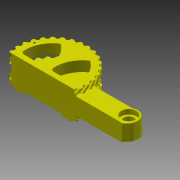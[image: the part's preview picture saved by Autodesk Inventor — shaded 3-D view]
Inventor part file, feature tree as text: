
AUTODESK INVENTOR PART (.ipt)
format: ipt  version: 2013 (Build 170138000, 138)  size: 5,737,472 bytes
history: native  units: mm
features: extrude x13, sketch x13, other x3, fillet x1
ambient origin geometry x8: Origin, YZ Plane, XZ Plane, XY Plane, X Axis, Y Axis, Z Axis, Center Point
bodies: Solid1 (feature_tree)
feature tree (30):
  other  "_GEARS.iam"
  other  "gear.ipt:1"
  other  "gear.ipt:2"
  extrude  "Extrusion1"  Depth=7.5mm TaperAngle=0.0deg
  extrude  "Extrusion2"  Depth=15.0mm
  extrude  "Extrusion3"  Depth=10.0mm TaperAngle=0.0deg
  extrude  "Extrusion4"  Depth=7.5mm
  extrude  "Extrusion5"  Depth=35.0mm
  extrude  "Extrusion6"  TaperAngle=135.0deg  [1 undecoded]
  extrude  "Extrusion7"  Depth=100.0mm
  extrude  "Extrusion11"  Depth=7.5mm
  extrude  "Extrusion30"  Depth=7.5mm
  extrude  "Extrusion32"  Depth=5.0mm
  extrude  "Extrusion33"  Depth=8.2mm
  extrude  "Extrusion34"  Depth=25.0mm TaperAngle=0.0deg
  extrude  "Extrusion35"  Depth=6.0mm TaperAngle=0.0deg
  fillet  "Fillet5"  Radius=7.5mm
  sketch  "Sketch1"  dims[d0=10.0mm d1=7.5mm d3=0.0mm]
  sketch  "Sketch2"  dims[d2=60.0mm d4=15.0mm]
  sketch  "Sketch3"  dims[d5=125.0mm d6=10.0mm d7=0.0mm]
  sketch  "Sketch4"  dims[d8=48.333333mm d10=7.5mm]
  sketch  "Sketch5"  dims[d11=15.0mm d12=35.0mm]
  sketch  "Sketch6"  dims[d13=27.5mm d14=135.0deg]
  sketch  "Sketch7"  dims[d15=112.5mm d16=100.0mm]
  sketch  "Sketch11"  dims[d17=25.0mm d18=0.0mm d19=7.5mm]
  sketch  "Sketch31"  dims[d21=25.0mm d22=0.0mm d23=7.5mm]
  sketch  "Sketch33"  dims[d24=40.0mm d25=5.0mm]
  sketch  "Sketch34"  dims[d26=25.0mm d27=0.0mm d28=8.2mm]
  sketch  "Sketch35"  dims[d30=35.0mm d31=25.0mm d32=0.0mm]
  sketch  "Sketch36"  dims[d33=13.2mm d34=6.0mm d35=0.0mm d36=7.5mm d38=3.5mm d39=0.0mm d54=80.0mm d56=43.75mm d57=10.0mm d58=0.0mm d140=15.1mm d142=3.0mm d143=0.0mm d148=22.1mm d150=7.0mm d151=0.0mm d152=7.0mm d153=0.0mm d154=3.0mm d155=7.0mm d156=0.0mm d157=90.0mm d159=3.490659mm d161=3.1mm d162=7.0mm d163=0.0mm d164=1.5mm]
note: 1 required parameter value undecoded (feature->parameter linkage not recoverable at this tier; creation-order binding heuristic only, values carry confidence <= 0.55)
